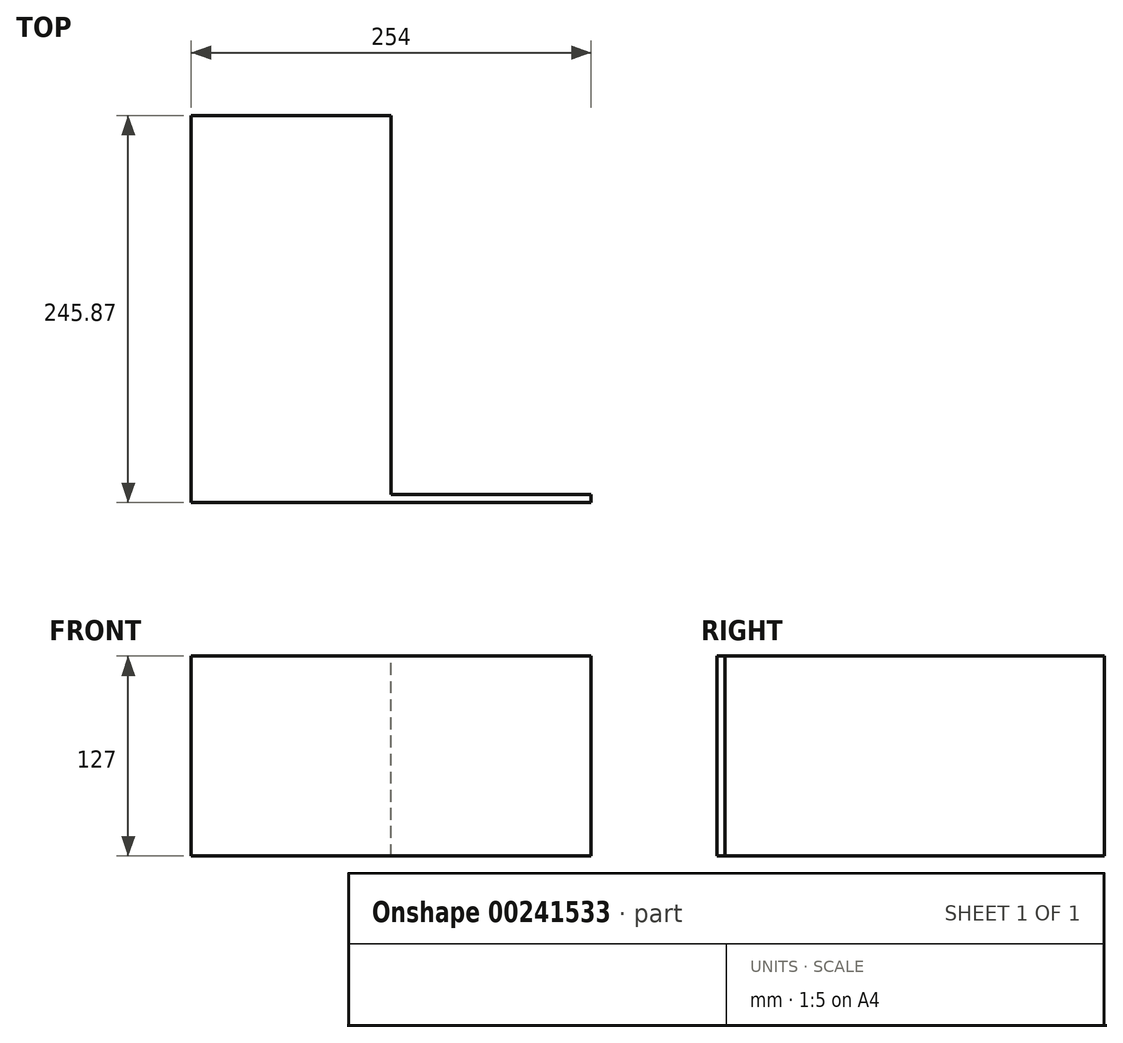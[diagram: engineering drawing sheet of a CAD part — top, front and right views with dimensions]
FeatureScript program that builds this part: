
annotation { "Feature Type Name" : "Feature", "Feature Type Description" : "" }
export const myFeature = defineFeature(function(context is Context, id is Id, definition is map)
    precondition{}
    {
        {
            assignVariable(context, id + "F0", {"name" : "A1", "anyValue" : 5});
        }
        {
            var Q0;
            Q0=qCreatedBy(makeId("Front.planeOp"),FACE);
            var sketch = newSketch(context, id + "F1", { "sketchPlane" : qUnion([Q0])});
            skLineSegment(sketch, "E0.bottom", {"start": v(-122.73, -99.32) * mm, "end": v(4.27, -99.32) * mm});
            skLineSegment(sketch, "E0.top", {"start": v(-122.73, 27.68) * mm, "end": v(4.27, 27.68) * mm});
            skLineSegment(sketch, "E0.left", {"start": v(-122.73, -99.32) * mm, "end": v(-122.73, 27.68) * mm});
            skLineSegment(sketch, "E0.right", {"start": v(4.27, -99.32) * mm, "end": v(4.27, 27.68) * mm});
            skSolve(sketch);
        }
        {
            var Q0;
            Q0=makeQuery(id+"F1.imprint","IMPRINT",FACE,{"disambiguationData":[TD([[makeQuery(id+"F1.imprint","IMPRINT",EDGE,{"derivedFrom":sQuery(id+"F1.wireOp",EDGE,"E0.bottom")}),1.0]])]});
            extrude(context, id + "F2", {"entities" : qUnion([Q0]), "depth" : (getVariable(context, 'A1')) * mm});
        }
        {
            var Q0;
            Q0=makeQuery(id+"F2.opExtrude","CAP_FACE",FACE,{"disambiguationData":[OSD([sQuery(id+"F1.wireOp",EDGE,"E0.bottom"),sQuery(id+"F1.wireOp",EDGE,"E0.top"),sQuery(id+"F1.wireOp",EDGE,"E0.left"),sQuery(id+"F1.wireOp",EDGE,"E0.right")])],"isStart":false});
            var sketch = newSketch(context, id + "F3", { "sketchPlane" : qUnion([Q0])});
            skLineSegment(sketch, "E1.bottom", {"start": v(-122.73, -99.32) * mm, "end": v(-249.73, -99.32) * mm});
            skLineSegment(sketch, "E1.top", {"start": v(-122.73, 27.68) * mm, "end": v(-249.73, 27.68) * mm});
            skLineSegment(sketch, "E1.left", {"start": v(-122.73, -99.32) * mm, "end": v(-122.73, 27.68) * mm});
            skLineSegment(sketch, "E1.right", {"start": v(-249.73, -99.32) * mm, "end": v(-249.73, 27.68) * mm});
            skSolve(sketch);
        }
        {
            var Q0;
            Q0=makeQuery(id+"F3.imprint","IMPRINT",FACE,{"disambiguationData":[TD([[makeQuery(id+"F3.imprint","IMPRINT",EDGE,{"derivedFrom":sQuery(id+"F3.wireOp",EDGE,"E1.bottom")}),-1.0]])]});
            extrude(context, id + "F4", {"entities" : qUnion([Q0]), "operationType" : NewBodyOperationType.ADD, "oppositeDirection" : true, "depth" : 245.87 * mm});
        }
    });
